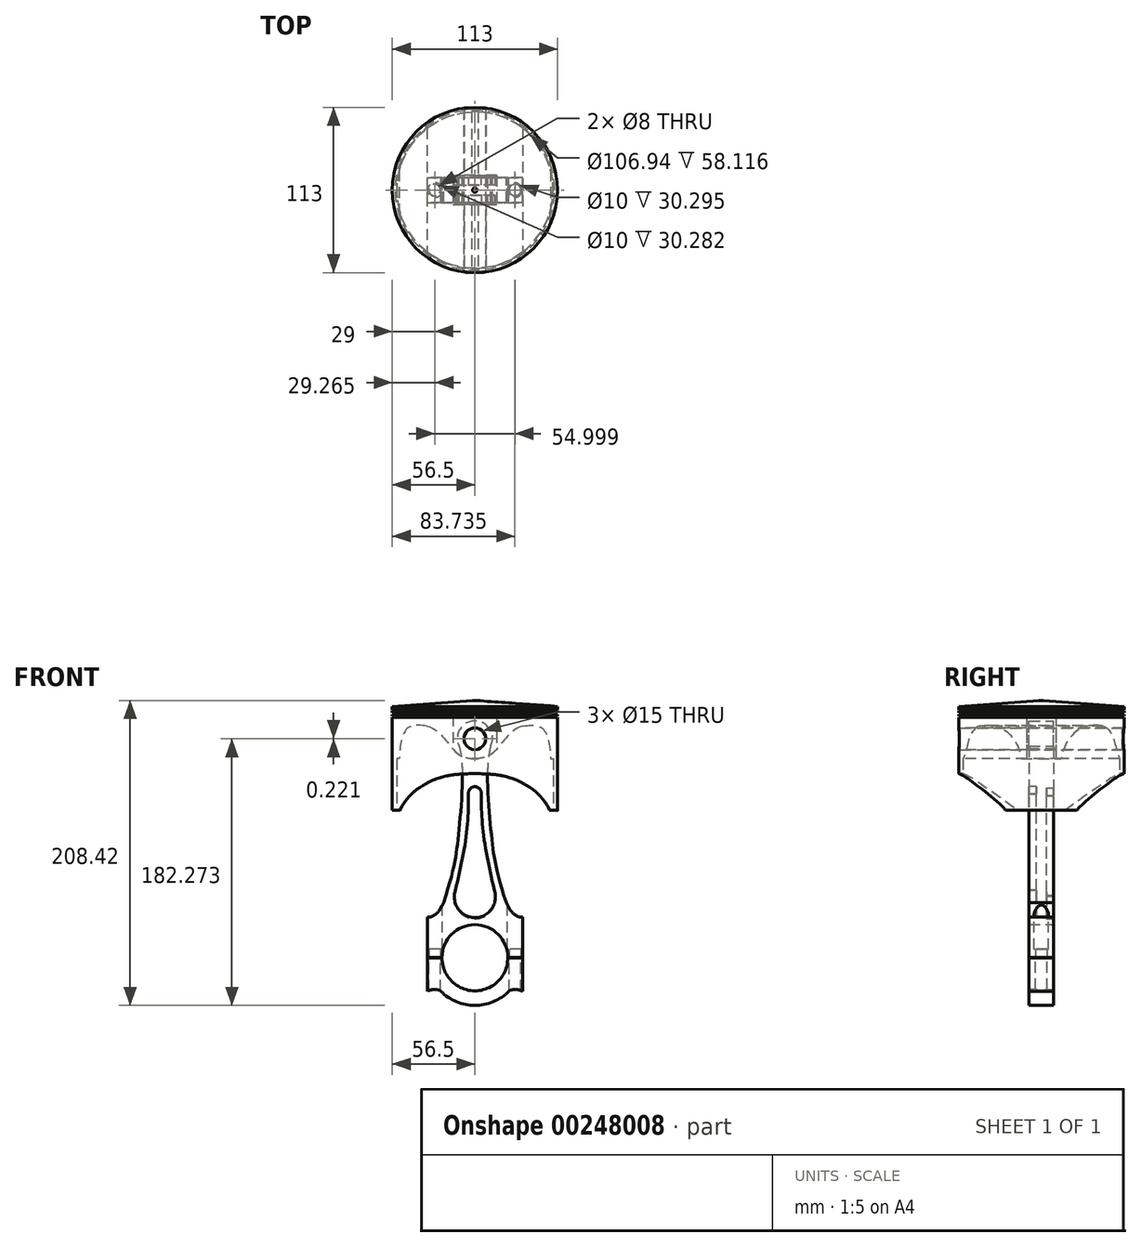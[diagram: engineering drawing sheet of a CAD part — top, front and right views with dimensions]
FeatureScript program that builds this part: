
annotation { "Feature Type Name" : "Feature", "Feature Type Description" : "" }
export const myFeature = defineFeature(function(context is Context, id is Id, definition is map)
    precondition{}
    {
        {
            var Q0;
            Q0=qCreatedBy(makeId("Top.planeOp"),FACE);
            var sketch = newSketch(context, id + "F0", { "sketchPlane" : qUnion([Q0])});
            skCircle(sketch, "E0", {"center": v(0, 0) * mm, "radius": 56.5 * mm});
            skSolve(sketch);
        }
        {
            var Q0;
            Q0 = qSketchRegion(id + "F0", true);
            extrude(context, id + "F1", {"entities" : qUnion([Q0]), "depth" : 75 * mm});
        }
        {
            var Q0;
            Q0=qCreatedBy(makeId("Front.planeOp"),FACE);
            var sketch = newSketch(context, id + "F2", { "sketchPlane" : qUnion([Q0])});
            skLineSegment(sketch, "E1.bottom", {"start": v(-56.6, 68.62) * mm, "end": v(-54.6, 68.62) * mm});
            skLineSegment(sketch, "E1.top", {"start": v(-56.6, 67.87) * mm, "end": v(-54.6, 67.87) * mm});
            skLineSegment(sketch, "E1.left", {"start": v(-56.6, 68.62) * mm, "end": v(-56.6, 67.87) * mm});
            skLineSegment(sketch, "E1.right", {"start": v(-54.6, 68.62) * mm, "end": v(-54.6, 67.87) * mm});
            skLineSegment(sketch, "E2.bottom", {"start": v(-56.6, 66.87) * mm, "end": v(-54.6, 66.87) * mm});
            skLineSegment(sketch, "E2.top", {"start": v(-56.6, 65.37) * mm, "end": v(-54.6, 65.37) * mm});
            skLineSegment(sketch, "E2.left", {"start": v(-56.6, 66.87) * mm, "end": v(-56.6, 65.37) * mm});
            skLineSegment(sketch, "E2.right", {"start": v(-54.6, 66.87) * mm, "end": v(-54.6, 65.37) * mm});
            skLineSegment(sketch, "E3.bottom", {"start": v(-56.6, 64.37) * mm, "end": v(-54.6, 64.37) * mm});
            skLineSegment(sketch, "E3.top", {"start": v(-56.6, 63.62) * mm, "end": v(-54.6, 63.62) * mm});
            skLineSegment(sketch, "E3.left", {"start": v(-56.6, 64.37) * mm, "end": v(-56.6, 63.62) * mm});
            skLineSegment(sketch, "E3.right", {"start": v(-54.6, 64.37) * mm, "end": v(-54.6, 63.62) * mm});
            skLineSegment(sketch, "E4", {"start": v(0, 50.95) * mm, "end": v(0, 87.92) * mm, "construction": true});
            skSolve(sketch);
        }
        {
            var Q0;
            Q0 = qSketchRegion(id + "F2", true);
            var Q1;
            Q1=sQuery(id+"F2.wireOp",EDGE,"E4");
            revolve(context, id + "F3", {"operationType" : NewBodyOperationType.REMOVE, "entities" : qUnion([Q0]), "axis" : qUnion([Q1]), "revolveType" : RevolveType.FULL, "oppositeDirection" : true});
        }
        {
            var Q0;
            Q0=makeQuery(id+"F1.opExtrude","CAP_EDGE",EDGE,{"disambiguationData":[OSD([sQuery(id+"F0.wireOp",EDGE,"E0")])],"isStart":false});
            chamfer(context, id + "F4", {"entities" : qUnion([Q0]), "chamferType" : ChamferType.TWO_OFFSETS, "width1" : 55 * mm, "oppositeDirection" : false, "width2" : 4 * mm, "tangentPropagation" : true});
        }
        {
            var Q0;
            Q0=qCreatedBy(makeId("Front.planeOp"),FACE);
            var sketch = newSketch(context, id + "F5", { "sketchPlane" : qUnion([Q0])});
            skFitSpline(sketch, "E5", {"points": [v(-51.03, 0) * mm, v(-25.4, 21.82) * mm, v(0, 25.06) * mm], "startDerivative": vector(24.82, 61.32) * mm, "endDerivative": vector(55.34, 1.1) * mm});
            skLineSegment(sketch, "E6", {"start": v(0, 0) * mm, "end": v(0, 25.06) * mm, "construction": true});
            skFitSpline(sketch, "E7.MirrorCS", {"points": [v(51.03, 0) * mm, v(25.4, 21.82) * mm, v(0, 25.06) * mm], "startDerivative": vector(-24.82, 61.32) * mm, "endDerivative": vector(-55.34, 1.1) * mm});
            skCircle(sketch, "E8", {"center": v(0, 48.85) * mm, "radius": 7.5 * mm});
            skLineSegment(sketch, "E9", {"start": v(-51.03, 0) * mm, "end": v(51.03, 0) * mm});
            skSolve(sketch);
        }
        {
            var Q0;
            Q0 = qSketchRegion(id + "F5", true);
            extrude(context, id + "F6", {"entities" : qUnion([Q0]), "operationType" : NewBodyOperationType.REMOVE, "endBound" : BoundingType.SYMMETRIC, "oppositeDirection" : true, "depth" : 200 * mm});
        }
        {
            var Q0;
            {var subQ0=sQuery(id+"F0.wireOp",EDGE,"E0");Q0=makeQuery(id+"F6.boolean.opBoolean","SPLIT",FACE,{"disambiguationData":[TD([makeQuery(id+"F6.opExtrude","SWEPT_FACE",FACE,{"disambiguationData":[OSD([sQuery(id+"F5.wireOp",EDGE,"E5")])]})])],"derivedFrom":makeQuery(id+"F1.opExtrude","CAP_FACE",FACE,{"disambiguationData":[OSD([subQ0])],"isStart":true})});}
            var sketch = newSketch(context, id + "F7", { "sketchPlane" : qUnion([Q0])});
            skCircle(sketch, "E10", {"center": v(0, 0) * mm, "radius": 53.47 * mm});
            skSolve(sketch);
        }
        {
            var Q0;
            Q0 = qSketchRegion(id + "F7", true);
            extrude(context, id + "F8", {"entities" : qUnion([Q0]), "operationType" : NewBodyOperationType.REMOVE, "oppositeDirection" : true, "depth" : 35.3 * mm});
        }
        {
            var Q0;
            Q0=qCreatedBy(makeId("Front.planeOp"),FACE);
            var sketch = newSketch(context, id + "F9", { "sketchPlane" : qUnion([Q0])});
            skFitSpline(sketch, "E11", {"points": [v(-32.64, 57.54) * mm, v(-12.31, 39.26) * mm, v(0, 34.97) * mm], "startDerivative": vector(50.47, -14.56) * mm, "endDerivative": vector(30.43, -4.8) * mm});
            skFitSpline(sketch, "E12.MirrorCS", {"points": [v(32.64, 57.54) * mm, v(12.31, 39.26) * mm, v(0, 34.97) * mm], "startDerivative": vector(-50.47, -14.56) * mm, "endDerivative": vector(-30.43, -4.8) * mm});
            skFitSpline(sketch, "E13", {"points": [v(-32.64, 57.54) * mm, v(-46.81, 55.3) * mm, v(-50.77, 0) * mm], "startDerivative": vector(-48.12, 6.31) * mm, "endDerivative": vector(5.99, -108.89) * mm});
            skFitSpline(sketch, "E14.MirrorCS", {"points": [v(32.64, 57.54) * mm, v(46.81, 55.3) * mm, v(50.77, 0) * mm], "startDerivative": vector(48.12, 6.31) * mm, "endDerivative": vector(-5.99, -108.89) * mm});
            skLineSegment(sketch, "E15", {"start": v(-50.77, 0) * mm, "end": v(50.77, 0) * mm});
            skSolve(sketch);
        }
        {
            var Q0;
            Q0 = qSketchRegion(id + "F9", true);
            var Q1;
            Q1=makeQuery(id+"F8.boolean.opBoolean","COPY",FACE,{"derivedFrom":makeQuery(id+"F8.opExtrude","SWEPT_FACE",FACE,{"disambiguationData":[OSD([sQuery(id+"F7.wireOp",EDGE,"E10")])]})});
            extrude(context, id + "F10", {"entities" : qUnion([Q0]), "operationType" : NewBodyOperationType.REMOVE, "endBound" : BoundingType.UP_TO_SURFACE, "oppositeDirection" : true, "endBoundEntityFace" : qUnion([Q1]), "depth" : 25 * mm});
        }
        {
            var Q0;
            Q0 = qSketchRegion(id + "F9", true);
            var Q1;
            {var subQ0=sQuery(id+"F7.wireOp",EDGE,"E10");Q1=makeQuery(id+"F10.boolean.opBoolean","MERGE",FACE,{"derivedFrom":[makeQuery(id+"F8.boolean.opBoolean","COPY",FACE,{"derivedFrom":makeQuery(id+"F8.opExtrude","SWEPT_FACE",FACE,{"disambiguationData":[OSD([subQ0])]})}),makeQuery(id+"F10.opExtrude","CAP_FACE",FACE,{"disambiguationData":[OSD([subQ0])],"isStart":false})]});}
            extrude(context, id + "F11", {"entities" : qUnion([Q0]), "operationType" : NewBodyOperationType.REMOVE, "endBound" : BoundingType.UP_TO_SURFACE, "endBoundEntityFace" : qUnion([Q1]), "depth" : 25 * mm});
        }
        {
            var Q0;
            Q0=qCreatedBy(makeId("Top.planeOp"),FACE);
            var sketch = newSketch(context, id + "F12", { "sketchPlane" : qUnion([Q0])});
            skLineSegment(sketch, "E16.bottom", {"start": v(-15, -10) * mm, "end": v(15, -10) * mm});
            skLineSegment(sketch, "E16.top", {"start": v(-15, 10) * mm, "end": v(15, 10) * mm});
            skLineSegment(sketch, "E16.left", {"start": v(-15, -10) * mm, "end": v(-15, 10) * mm});
            skLineSegment(sketch, "E16.right", {"start": v(15, -10) * mm, "end": v(15, 10) * mm});
            skSolve(sketch);
        }
        {
            var Q0;
            Q0 = qSketchRegion(id + "F12", true);
            extrude(context, id + "F13", {"entities" : qUnion([Q0]), "operationType" : NewBodyOperationType.REMOVE, "depth" : 65 * mm});
        }
        {
            var Q0;
            Q0=qCreatedBy(makeId("Front.planeOp"),FACE);
            var sketch = newSketch(context, id + "F14", { "sketchPlane" : qUnion([Q0])});
            skCircle(sketch, "E17", {"center": v(0, 49.07) * mm, "radius": 7.5 * mm});
            skCircle(sketch, "E18", {"center": v(0, 49.07) * mm, "radius": 12 * mm});
            skFitSpline(sketch, "E19", {"points": [v(10.8, 43.85) * mm, v(11.16, -15.93) * mm, v(29.22, -86.45) * mm], "startDerivative": vector(-26.49, -88.2) * mm, "endDerivative": vector(85.7, -248.74) * mm});
            skFitSpline(sketch, "E20.MirrorCS", {"points": [v(-10.8, 43.85) * mm, v(-11.16, -15.93) * mm, v(-29.22, -86.45) * mm], "startDerivative": vector(26.49, -88.2) * mm, "endDerivative": vector(-85.7, -248.74) * mm});
            skPoint(sketch, "E21.orphan", {"position": v(44.1, -162) * mm});
            skLineSegment(sketch, "E22", {"start": v(0, 25.7) * mm, "end": v(96.4, 25.7) * mm, "construction": true});
            skLineSegment(sketch, "E23", {"start": v(99.38, -79.3) * mm, "end": v(-45.84, -79.3) * mm, "construction": true});
            skArc(sketch, "E24", {"start": v(22.5, -100.68) * mm, "mid": v(0, -78.18) * mm, "end": v(-22.5, -100.68) * mm});
            skArc(sketch, "E25", {"start": v(32.5, -100.68) * mm, "mid": v(0, -68.18) * mm, "end": v(-32.5, -100.68) * mm});
            skLineSegment(sketch, "E26", {"start": v(22.5, -100.68) * mm, "end": v(32.5, -100.68) * mm});
            skLineSegment(sketch, "E27", {"start": v(-22.5, -100.68) * mm, "end": v(-32.5, -100.68) * mm});
            skLineSegment(sketch, "E28", {"start": v(-32.5, -100.68) * mm, "end": v(-32.5, -73.1) * mm});
            skFitSpline(sketch, "E29", {"points": [v(-32.5, -73.1) * mm, v(-21.41, -63.14) * mm], "startDerivative": vector(18.38, 0) * mm, "endDerivative": vector(7.88, 15.05) * mm});
            skLineSegment(sketch, "E30", {"start": v(0, -100.68) * mm, "end": v(0, -50.1) * mm, "construction": true});
            skFitSpline(sketch, "E31.MirrorCS", {"points": [v(32.5, -73.1) * mm, v(21.41, -63.14) * mm], "startDerivative": vector(-18.38, 0) * mm, "endDerivative": vector(-7.88, 15.05) * mm});
            skLineSegment(sketch, "E32.MirrorCS", {"start": v(32.5, -100.68) * mm, "end": v(32.5, -73.1) * mm});
            skSolve(sketch);
        }
        {
            var Q0;
            Q0 = qSketchRegion(id + "F14", true);
            extrude(context, id + "F15", {"entities" : qUnion([Q0]), "endBound" : BoundingType.SYMMETRIC, "depth" : 17 * mm});
        }
        {
            var Q0;
            Q0=makeQuery(id+"F15.opExtrude","CAP_FACE",FACE,{"disambiguationData":[OSD([sQuery(id+"F14.wireOp",EDGE,"E17"),sQuery(id+"F14.wireOp",EDGE,"E18"),sQuery(id+"F14.wireOp",EDGE,"E19"),sQuery(id+"F14.wireOp",EDGE,"E20.MirrorCS"),sQuery(id+"F14.wireOp",EDGE,"E24"),sQuery(id+"F14.wireOp",EDGE,"E25"),sQuery(id+"F14.wireOp",EDGE,"E26"),sQuery(id+"F14.wireOp",EDGE,"E27")])],"isStart":false});
            var sketch = newSketch(context, id + "F16", { "sketchPlane" : qUnion([Q0])});
            skArc(sketch, "E33", {"start": v(4.26, 10.72) * mm, "mid": v(0.2, 16.16) * mm, "end": v(-4.34, 11.12) * mm});
            skArc(sketch, "E34", {"start": v(-13.37, -55) * mm, "mid": v(0.22, -73.34) * mm, "end": v(13.23, -54.58) * mm});
            skFitSpline(sketch, "E35", {"points": [v(-13.9, -57.26) * mm, v(-5.9, -17.35) * mm, v(-4.34, 11.12) * mm], "startDerivative": vector(17.74, 76.27) * mm, "endDerivative": vector(0.84, 60.02) * mm});
            skFitSpline(sketch, "E36", {"points": [v(13.97, -57.9) * mm, v(5.9, -16.65) * mm, v(4.26, 10.72) * mm], "startDerivative": vector(-17.6, 78.25) * mm, "endDerivative": vector(-1.24, 58.29) * mm});
            skSolve(sketch);
        }
        {
            var Q0;
            Q0 = qSketchRegion(id + "F16", true);
            extrude(context, id + "F17", {"entities" : qUnion([Q0]), "operationType" : NewBodyOperationType.REMOVE, "oppositeDirection" : true, "depth" : 5 * mm});
        }
        {
            var Q0;
            Q0=makeQuery(id+"F15.opExtrude","CAP_FACE",FACE,{"disambiguationData":[OSD([sQuery(id+"F14.wireOp",EDGE,"E17"),sQuery(id+"F14.wireOp",EDGE,"E18"),sQuery(id+"F14.wireOp",EDGE,"E19"),sQuery(id+"F14.wireOp",EDGE,"E20.MirrorCS"),sQuery(id+"F14.wireOp",EDGE,"E24"),sQuery(id+"F14.wireOp",EDGE,"E25"),sQuery(id+"F14.wireOp",EDGE,"E26"),sQuery(id+"F14.wireOp",EDGE,"E27")])],"isStart":true});
            var sketch = newSketch(context, id + "F18", { "sketchPlane" : qUnion([Q0])});
            skArc(sketch, "E37", {"start": v(4.17, 9.83) * mm, "mid": v(0.12, 15.28) * mm, "end": v(-4.42, 10.24) * mm});
            skArc(sketch, "E38", {"start": v(-13.45, -55.89) * mm, "mid": v(0.14, -74.23) * mm, "end": v(13.14, -55.47) * mm});
            skFitSpline(sketch, "E39", {"points": [v(-13.98, -58.15) * mm, v(-5.98, -18.23) * mm, v(-4.42, 10.24) * mm], "startDerivative": vector(17.74, 76.27) * mm, "endDerivative": vector(0.84, 60.02) * mm});
            skFitSpline(sketch, "E40", {"points": [v(13.89, -58.79) * mm, v(5.81, -17.54) * mm, v(4.17, 9.83) * mm], "startDerivative": vector(-17.6, 78.25) * mm, "endDerivative": vector(-1.24, 58.29) * mm});
            skSolve(sketch);
        }
        {
            var Q0;
            {var subQ6=sQuery(id+"F18.wireOp",EDGE,"E37");Q0=makeQuery(id+"F18.imprint","IMPRINT",FACE,{"disambiguationData":[TD([[makeQuery(id+"F18.imprint","IMPRINT",EDGE,{"derivedFrom":subQ6}),1.0]])]});}
            extrude(context, id + "F19", {"entities" : qUnion([Q0]), "operationType" : NewBodyOperationType.REMOVE, "oppositeDirection" : true, "depth" : 5 * mm});
        }
        {
            var Q0;
            Q0=qCreatedBy(makeId("Top.planeOp"),FACE);
            var sketch = newSketch(context, id + "F20", { "sketchPlane" : qUnion([Q0])});
            skCircle(sketch, "E41", {"center": v(-27.23, 0) * mm, "radius": 5 * mm});
            skLineSegment(sketch, "E42", {"start": v(0, -18.79) * mm, "end": v(0, 19.9) * mm, "construction": true});
            skCircle(sketch, "E43.MirrorC", {"center": v(27.23, 0) * mm, "radius": 5 * mm});
            skSolve(sketch);
        }
        {
            var Q0;
            Q0 = qSketchRegion(id + "F20", true);
            extrude(context, id + "F21", {"entities" : qUnion([Q0]), "operationType" : NewBodyOperationType.REMOVE, "oppositeDirection" : true, "depth" : 95 * mm});
        }
        {
            var Q0;
            Q0=makeQuery(id+"F15.opExtrude","SWEPT_FACE",FACE,{"disambiguationData":[OSD([sQuery(id+"F14.wireOp",EDGE,"E27")])]});
            var sketch = newSketch(context, id + "F22", { "sketchPlane" : qUnion([Q0])});
            skCircle(sketch, "E44", {"center": v(-27.5, 0) * mm, "radius": 4 * mm});
            skLineSegment(sketch, "E45", {"start": v(0, 22.07) * mm, "end": v(0, -18.52) * mm, "construction": true});
            skCircle(sketch, "E46.MirrorC", {"center": v(27.5, 0) * mm, "radius": 4 * mm});
            skSolve(sketch);
        }
        {
            var Q0;
            Q0 = qSketchRegion(id + "F22", true);
            extrude(context, id + "F23", {"entities" : qUnion([Q0]), "operationType" : NewBodyOperationType.REMOVE, "endBound" : BoundingType.SYMMETRIC, "oppositeDirection" : true, "depth" : 25 * mm});
        }
        {
            var Q0;
            Q0=qCreatedBy(makeId("Front.planeOp"),FACE);
            var sketch = newSketch(context, id + "F24", { "sketchPlane" : qUnion([Q0])});
            skArc(sketch, "E47", {"start": v(-22.5, -100.8) * mm, "mid": v(0, -123.42) * mm, "end": v(22.5, -100.8) * mm});
            skArc(sketch, "E48", {"start": v(-32.5, -100.8) * mm, "mid": v(-32.5, -100.92) * mm, "end": v(-32.5, -101.05) * mm});
            skLineSegment(sketch, "E49", {"start": v(-32.5, -100.8) * mm, "end": v(-22.5, -100.8) * mm});
            skLineSegment(sketch, "E50", {"start": v(22.5, -100.8) * mm, "end": v(32.5, -100.8) * mm});
            skLineSegment(sketch, "E51", {"start": v(-32.5, -100.8) * mm, "end": v(-32.5, -123.65) * mm});
            skFitSpline(sketch, "E52", {"points": [v(-32.5, -123.65) * mm, v(-23.23, -123.65) * mm], "startDerivative": vector(10.66, 5.63) * mm, "endDerivative": vector(3.35, -3.6) * mm});
            skArc(sketch, "E53.trimOffspring", {"start": v(-23.23, -123.65) * mm, "mid": v(0, -133.42) * mm, "end": v(23.23, -123.65) * mm});
            skLineSegment(sketch, "E54", {"start": v(0, -100.92) * mm, "end": v(0, -141.57) * mm, "construction": true});
            skFitSpline(sketch, "E55.MirrorCS", {"points": [v(32.5, -123.65) * mm, v(23.23, -123.65) * mm], "startDerivative": vector(-10.66, 5.63) * mm, "endDerivative": vector(-3.35, -3.6) * mm});
            skLineSegment(sketch, "E56.MirrorCS", {"start": v(32.5, -100.8) * mm, "end": v(32.5, -123.65) * mm});
            skArc(sketch, "E57.trimOffspring", {"start": v(32.5, -101.05) * mm, "mid": v(32.5, -100.92) * mm, "end": v(32.5, -100.8) * mm});
            skSolve(sketch);
        }
        {
            var Q0;
            Q0 = qSketchRegion(id + "F24", true);
            extrude(context, id + "F25", {"entities" : qUnion([Q0]), "endBound" : BoundingType.SYMMETRIC, "depth" : 17 * mm});
        }
        {
            var Q0;
            Q0=makeQuery(id+"F25.opExtrude","SWEPT_FACE",FACE,{"disambiguationData":[OSD([sQuery(id+"F24.wireOp",EDGE,"E49")])]});
            var sketch = newSketch(context, id + "F26", { "sketchPlane" : qUnion([Q0])});
            skCircle(sketch, "E58", {"center": v(-27.5, 0) * mm, "radius": 4 * mm});
            skLineSegment(sketch, "E59", {"start": v(-27.5, 8.5) * mm, "end": v(-27.5, -2.5) * mm, "construction": true});
            skLineSegment(sketch, "E60", {"start": v(0, 10.3) * mm, "end": v(0, -10.98) * mm, "construction": true});
            skCircle(sketch, "E61.MirrorC", {"center": v(27.5, 0) * mm, "radius": 4 * mm});
            skSolve(sketch);
        }
        {
            var Q0;
            Q0 = qSketchRegion(id + "F26", true);
            extrude(context, id + "F27", {"entities" : qUnion([Q0]), "operationType" : NewBodyOperationType.REMOVE, "oppositeDirection" : true, "depth" : 25 * mm});
        }
        {
            var Q0;
            Q0=qCreatedBy(makeId("Front.planeOp"),FACE);
            var sketch = newSketch(context, id + "F28", { "sketchPlane" : qUnion([Q0])});
            skCircle(sketch, "E62", {"center": v(0, 48.75) * mm, "radius": 7.5 * mm});
            skSolve(sketch);
        }
        {
            var Q0;
            Q0 = qSketchRegion(id + "F28", true);
            extrude(context, id + "F29", {"entities" : qUnion([Q0]), "endBound" : BoundingType.SYMMETRIC, "depth" : 111 * mm});
        }
    });
